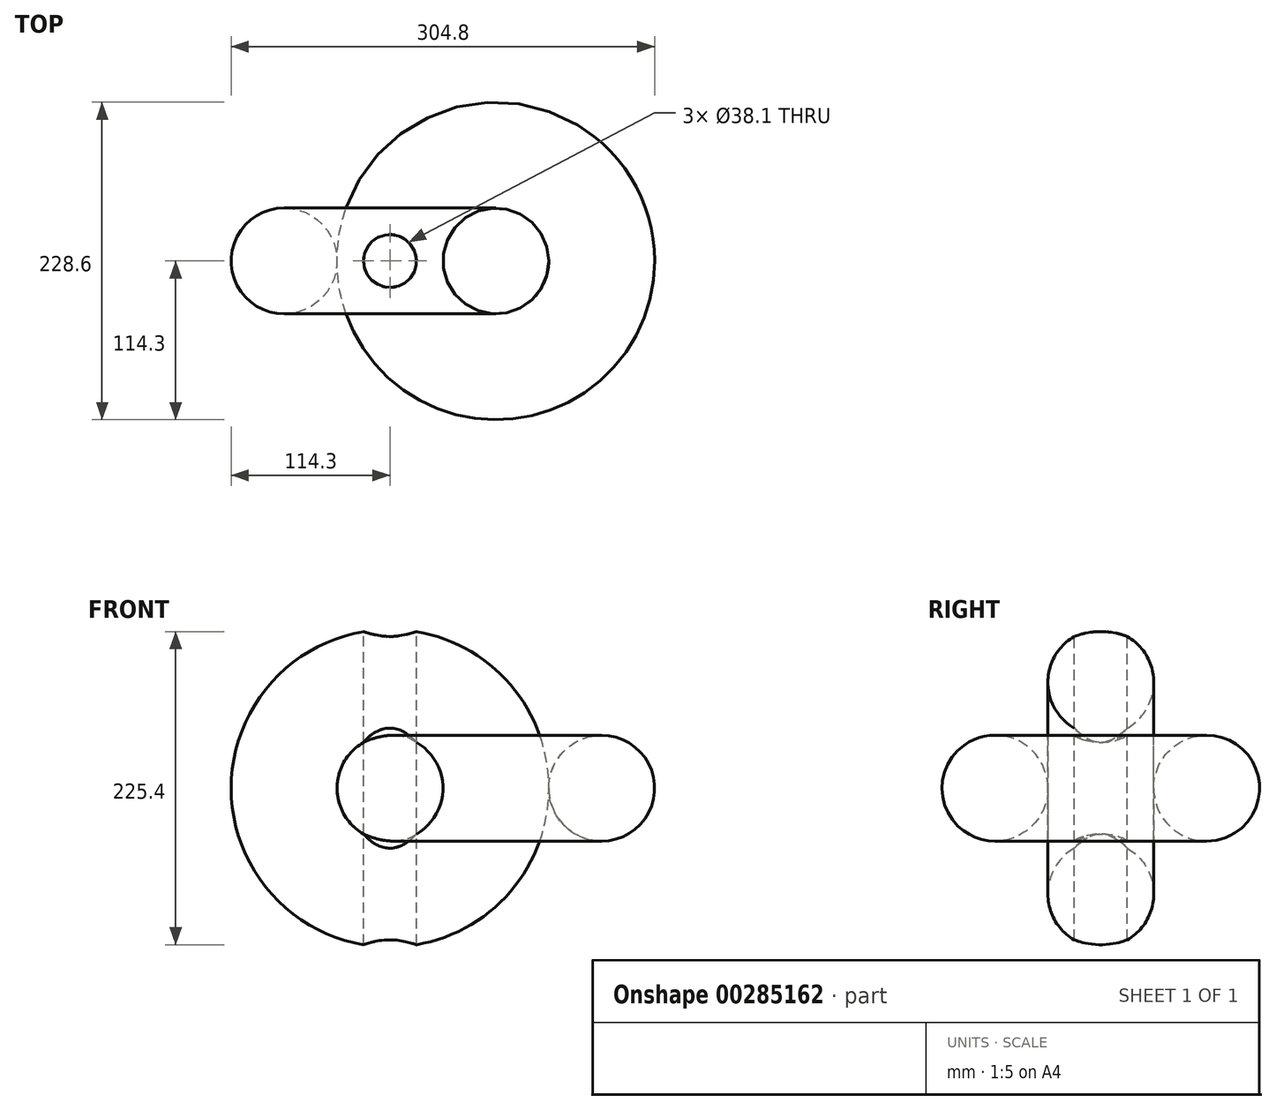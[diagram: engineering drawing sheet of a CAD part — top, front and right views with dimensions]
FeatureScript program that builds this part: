
annotation { "Feature Type Name" : "Feature", "Feature Type Description" : "" }
export const myFeature = defineFeature(function(context is Context, id is Id, definition is map)
    precondition{}
    {
        {
            var Q0;
            Q0=qCreatedBy(makeId("Front.planeOp"),FACE);
            var sketch = newSketch(context, id + "F0", { "sketchPlane" : qUnion([Q0])});
            skCircle(sketch, "E0", {"center": v(0, 0) * mm, "radius": 38.1 * mm});
            skSolve(sketch);
        }
        {
            var Q0;
            Q0=qCreatedBy(makeId("Top.planeOp"),FACE);
            var sketch = newSketch(context, id + "F1", { "sketchPlane" : qUnion([Q0])});
            skCircle(sketch, "E1", {"center": v(76.2, 0) * mm, "radius": 38.1 * mm});
            skSolve(sketch);
        }
        {
            var Q0;
            Q0=makeQuery(id+"F0.imprint","IMPRINT",FACE,{"disambiguationData":[TD([[makeQuery(id+"F0.imprint","IMPRINT",EDGE,{"derivedFrom":sQuery(id+"F0.wireOp",EDGE,"E0")}),1.0]])]});
            var Q1;
            Q1=sQuery(id+"F1.wireOp",EDGE,"E1");
            revolve(context, id + "F2", {"entities" : qUnion([Q0]), "axis" : qUnion([Q1]), "revolveType" : RevolveType.FULL});
        }
        {
            var Q0;
            Q0=qCreatedBy(makeId("Top.planeOp"),FACE);
            var sketch = newSketch(context, id + "F3", { "sketchPlane" : qUnion([Q0])});
            skCircle(sketch, "E2", {"center": v(76.2, 0) * mm, "radius": 38.1 * mm});
            skSolve(sketch);
        }
        {
            var Q0;
            Q0 = qSketchRegion(id + "F3", true);
            var Q1;
            Q1=sQuery(id+"F0.wireOp",EDGE,"E0");
            revolve(context, id + "F4", {"operationType" : NewBodyOperationType.ADD, "entities" : qUnion([Q0]), "axis" : qUnion([Q1]), "revolveType" : RevolveType.FULL});
        }
        {
            var Q0;
            Q0=makeQuery(id+"F3.imprint","IMPRINT",FACE,{"disambiguationData":[TD([[makeQuery(id+"F3.imprint","IMPRINT",EDGE,{"derivedFrom":sQuery(id+"F3.wireOp",EDGE,"E2")}),1.0]])]});
            cPlane(context, id + "F5", {"entities" : qUnion([Q0]), "cplaneType" : CPlaneType.OFFSET, "offset" : 114.3 * mm, "width" : 152.4 * mm, "height" : 152.4 * mm});
        }
        {
            var Q0;
            Q0=qCreatedBy(id+"F5.planeOp",FACE);
            var sketch = newSketch(context, id + "F6", { "sketchPlane" : qUnion([Q0])});
            skCircle(sketch, "E3", {"center": v(0, 0) * mm, "radius": 19.05 * mm});
            skSolve(sketch);
        }
        {
            var Q0;
            Q0 = qSketchRegion(id + "F6", true);
            extrude(context, id + "F7", {"entities" : qUnion([Q0]), "operationType" : NewBodyOperationType.REMOVE, "endBound" : BoundingType.THROUGH_ALL, "oppositeDirection" : true, "depth" : 228.6 * mm});
        }
    });
